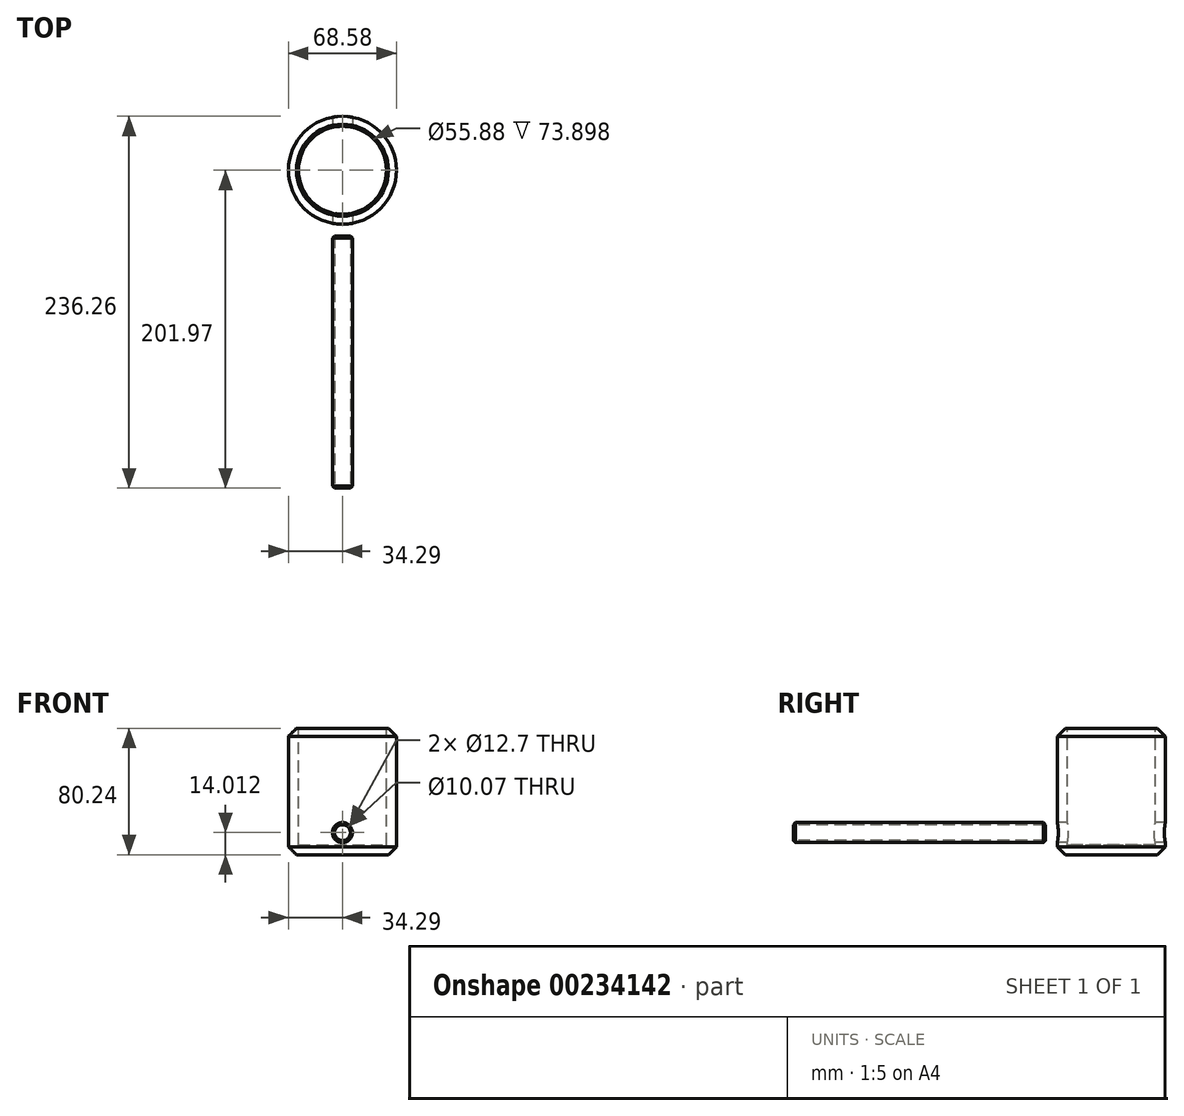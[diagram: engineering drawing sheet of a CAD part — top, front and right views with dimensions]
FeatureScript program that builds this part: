
annotation { "Feature Type Name" : "Feature", "Feature Type Description" : "" }
export const myFeature = defineFeature(function(context is Context, id is Id, definition is map)
    precondition{}
    {
        {
            var Q0;
            Q0=qCreatedBy(makeId("Front.planeOp"),FACE);
            var sketch = newSketch(context, id + "F0", { "sketchPlane" : qUnion([Q0])});
            skLineSegment(sketch, "E0.bottom", {"start": v(34.3, -40.12) * mm, "end": v(-34.3, -40.12) * mm});
            skLineSegment(sketch, "E0.top", {"start": v(34.29, 40.12) * mm, "end": v(-34.29, 40.12) * mm});
            skLineSegment(sketch, "E0.left", {"start": v(34.3, -40.12) * mm, "end": v(34.3, 40.12) * mm});
            skLineSegment(sketch, "E0.right", {"start": v(-34.3, -40.12) * mm, "end": v(-34.3, 40.12) * mm});
            skPoint(sketch, "E0.middle", {"position": v(0, 0) * mm});
            skLineSegment(sketch, "E1", {"start": v(0, 52.15) * mm, "end": v(0, -64.7) * mm});
            skPoint(sketch, "E1.endSnap0", {"position": v(0, -40.12) * mm});
            skSolve(sketch);
        }
        {
            var Q0;
            {var subQ0=sQuery(id+"F0.wireOp",EDGE,"E0.left");Q0=makeQuery(id+"F0.imprint","IMPRINT",FACE,{"disambiguationData":[TD([[makeQuery(id+"F0.imprint","IMPRINT",EDGE,{"derivedFrom":subQ0}),1.0]])]});}
            var sketch = newSketch(context, id + "F1", { "sketchPlane" : qUnion([Q0])});
            skSolve(sketch);
        }
        {
            var Q0;
            Q0 = qSketchRegion(id + "F1", true);
            var Q1;
            {var subQ0=sQuery(id+"F0.wireOp",EDGE,"E0.left");Q1=makeQuery(id+"F0.imprint","IMPRINT",FACE,{"disambiguationData":[TD([[makeQuery(id+"F0.imprint","IMPRINT",EDGE,{"derivedFrom":subQ0}),1.0]])]});}
            var Q2;
            Q2=sQuery(id+"F0.wireOp",EDGE,"E1");
            revolve(context, id + "F2", {"entities" : qUnion([Q0, Q1]), "axis" : qUnion([Q2]), "revolveType" : RevolveType.FULL});
        }
        {
            var Q0;
            Q0=qCreatedBy(makeId("Front.planeOp"),FACE);
            cPlane(context, id + "F3", {"entities" : qUnion([Q0]), "cplaneType" : CPlaneType.OFFSET, "offset" : 38.1 * mm, "width" : 152.4 * mm, "height" : 152.4 * mm});
        }
        {
            var Q0;
            Q0=qCreatedBy(id+"F3.planeOp",FACE);
            var sketch = newSketch(context, id + "F4", { "sketchPlane" : qUnion([Q0])});
            skCircle(sketch, "E2", {"center": v(0, -12.09) * mm, "radius": 6.35 * mm});
            skSolve(sketch);
        }
        {
            var Q0;
            Q0=makeQuery(id+"F2.opRevolve","SWEPT_FACE",FACE,{"disambiguationData":[OSD([sQuery(id+"F0.wireOp",EDGE,"E0.top")])]});
            shell(context, id + "F5", {"entities" : qUnion([Q0]), "thickness" : 6.35 * mm});
        }
        {
            var Q0;
            Q0=makeQuery(id+"F4.imprint","IMPRINT",FACE,{"disambiguationData":[TD([[makeQuery(id+"F4.imprint","IMPRINT",EDGE,{"derivedFrom":sQuery(id+"F4.wireOp",EDGE,"E2")}),1.0]])]});
            extrude(context, id + "F6", {"entities" : qUnion([Q0]), "operationType" : NewBodyOperationType.ADD, "depth" : 165.1 * mm});
        }
        {
            var Q0;
            Q0=qCreatedBy(id+"F3.planeOp",FACE);
            var sketch = newSketch(context, id + "F12", { "sketchPlane" : qUnion([Q0])});
            skCircle(sketch, "E3", {"center": v(0, -26.1) * mm, "radius": 6.35 * mm});
            skSolve(sketch);
        }
        {
            var Q0;
            Q0=makeQuery(id+"F12.imprint","IMPRINT",FACE,{"disambiguationData":[TD([[makeQuery(id+"F12.imprint","IMPRINT",EDGE,{"derivedFrom":sQuery(id+"F12.wireOp",EDGE,"E3")}),1.0]])]});
            extrude(context, id + "F7", {"entities" : qUnion([Q0]), "depth" : 165.1 * mm});
        }
        {
            var Q0;
            Q0=makeQuery(id+"F7.opExtrude","CAP_FACE",FACE,{"disambiguationData":[OSD([sQuery(id+"F12.wireOp",EDGE,"E3")])],"isStart":false});
            var sketch = newSketch(context, id + "F8", { "sketchPlane" : qUnion([Q0])});
            skCircle(sketch, "E4", {"center": v(0, -26.1) * mm, "radius": 5.04 * mm});
            skSolve(sketch);
        }
        {
            var Q0;
            Q0=makeQuery(id+"F8.imprint","IMPRINT",FACE,{"disambiguationData":[TD([[makeQuery(id+"F8.imprint","IMPRINT",EDGE,{"derivedFrom":sQuery(id+"F8.wireOp",EDGE,"E4")}),1.0]])]});
            extrude(context, id + "F13", {"entities" : qUnion([Q0]), "operationType" : NewBodyOperationType.REMOVE, "endBound" : BoundingType.THROUGH_ALL, "oppositeDirection" : true, "depth" : 25.4 * mm});
        }
        {
            var Q0;
            Q0=makeQuery(id+"F6.opExtrude","SWEPT_BODY",BODY,{"disambiguationData":[OSD([sQuery(id+"F4.wireOp",EDGE,"E2")])]});
            deleteBodies(context, id + "F9", {"entities" : qUnion([Q0])});
        }
        {
            var Q0;
            Q0=makeQuery(id+"F12.imprint","IMPRINT",FACE,{"disambiguationData":[TD([[makeQuery(id+"F12.imprint","IMPRINT",EDGE,{"derivedFrom":sQuery(id+"F12.wireOp",EDGE,"E3")}),1.0]])]});
            extrude(context, id + "F14", {"entities" : qUnion([Q0]), "operationType" : NewBodyOperationType.REMOVE, "endBound" : BoundingType.THROUGH_ALL, "oppositeDirection" : true, "depth" : 25.4 * mm});
        }
        {
            var Q0;
            Q0=makeQuery(id+"F7.opExtrude","CAP_EDGE",EDGE,{"disambiguationData":[OSD([sQuery(id+"F12.wireOp",EDGE,"E3")])],"isStart":false});
            chamfer(context, id + "F10", {"entities" : qUnion([Q0]), "width" : 2.54 * mm, "tangentPropagation" : true});
        }
        {
            var Q0;
            Q0=makeQuery(id+"F7.opExtrude","CAP_EDGE",EDGE,{"disambiguationData":[OSD([sQuery(id+"F12.wireOp",EDGE,"E3")])],"isStart":true});
            chamfer(context, id + "F15", {"entities" : qUnion([Q0]), "width" : 5.08 * mm, "tangentPropagation" : true});
        }
        {
            var Q0;
            Q0=makeQuery(id+"F2.opRevolve","SWEPT_EDGE",EDGE,{"disambiguationData":[OSD([sQuery(id+"F0.wireOp",EDGE,"E0.top"),sQuery(id+"F0.wireOp",EDGE,"E0.left")])]});
            chamfer(context, id + "F16", {"entities" : qUnion([Q0]), "width" : 5.08 * mm, "tangentPropagation" : true});
        }
        {
            var Q0;
            Q0=makeQuery(id+"F2.opRevolve","SWEPT_FACE",FACE,{"disambiguationData":[OSD([sQuery(id+"F0.wireOp",EDGE,"E0.bottom")])]});
            chamfer(context, id + "F11", {"entities" : qUnion([Q0]), "width" : 5.08 * mm, "tangentPropagation" : true});
        }
    });
